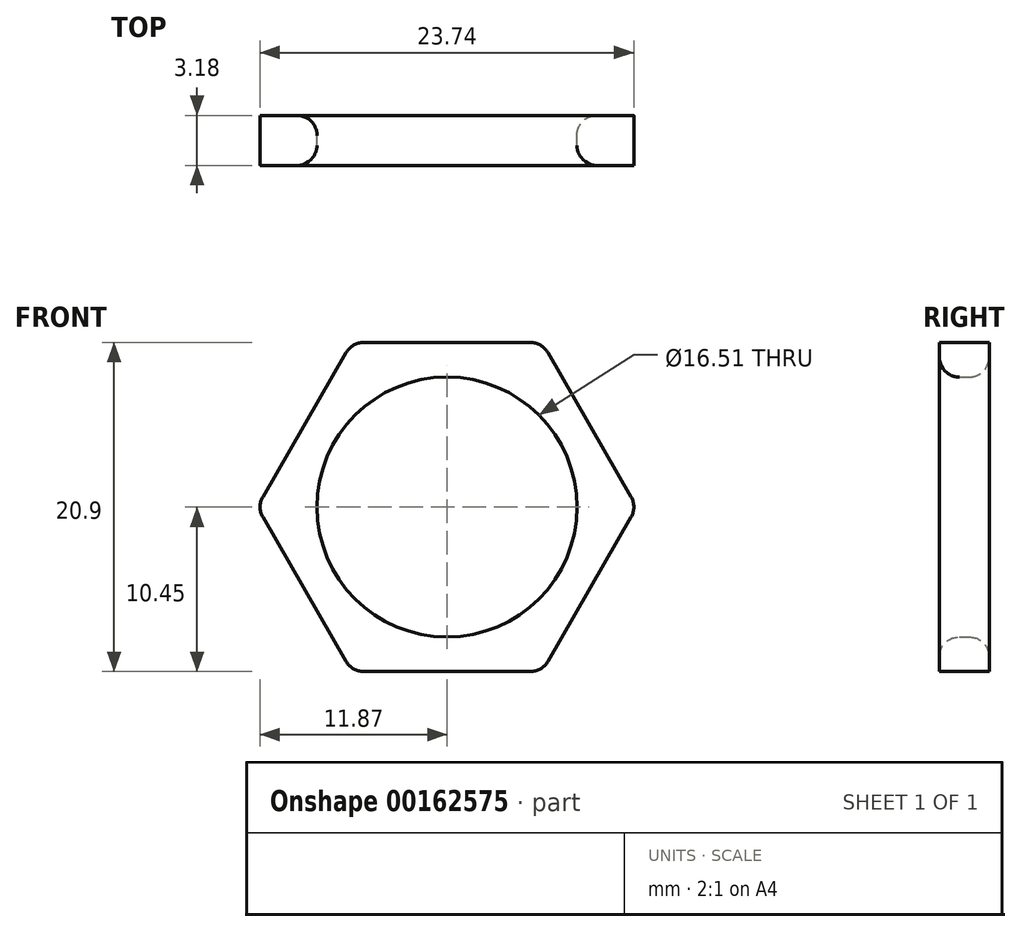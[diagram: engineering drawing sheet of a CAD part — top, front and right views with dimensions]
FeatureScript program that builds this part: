
annotation { "Feature Type Name" : "Feature", "Feature Type Description" : "" }
export const myFeature = defineFeature(function(context is Context, id is Id, definition is map)
    precondition{}
    {
        {
            var Q0;
            Q0=qCreatedBy(makeId("Front.planeOp"),FACE);
            var sketch = newSketch(context, id + "F0", { "sketchPlane" : qUnion([Q0])});
            skCircle(sketch, "E0.cCircle", {"center": v(0, 0) * mm, "radius": 12.07 * mm, "construction": true});
            skLineSegment(sketch, "E0.0", {"start": v(-12.06, 0) * mm, "end": v(-6.03, 10.45) * mm});
            skLineSegment(sketch, "E0.1", {"start": v(-6.03, 10.45) * mm, "end": v(6.03, 10.45) * mm});
            skLineSegment(sketch, "E0.2", {"start": v(6.03, 10.45) * mm, "end": v(12.07, 0) * mm});
            skLineSegment(sketch, "E0.3", {"start": v(12.06, 0) * mm, "end": v(6.03, -10.45) * mm});
            skLineSegment(sketch, "E0.4", {"start": v(6.03, -10.45) * mm, "end": v(-6.03, -10.45) * mm});
            skLineSegment(sketch, "E0.5", {"start": v(-6.03, -10.45) * mm, "end": v(-12.07, 0) * mm});
            skPoint(sketch, "E1.3.end.orphan", {"position": v(0, 8.28) * mm});
            skCircle(sketch, "E2", {"center": v(0, 0) * mm, "radius": 8.26 * mm});
            skSolve(sketch);
        }
        {
            var Q0;
            Q0 = qSketchRegion(id + "F0", true);
            extrude(context, id + "F2", {"entities" : qUnion([Q0]), "depth" : 3.17 * mm});
        }
        {
            var Q0;
            Q0=makeQuery(id+"F2.opExtrude","CAP_EDGE",EDGE,{"disambiguationData":[OSD([sQuery(id+"F0.wireOp",EDGE,"E2")])],"isStart":false});
            var Q1;
            Q1=makeQuery(id+"F2.opExtrude","CAP_EDGE",EDGE,{"disambiguationData":[OSD([sQuery(id+"F0.wireOp",EDGE,"E2")])],"isStart":true});
            var Q2;
            Q2=makeQuery(id+"F2.opExtrude","SWEPT_EDGE",EDGE,{"disambiguationData":[OSD([sQuery(id+"F0.wireOp",EDGE,"E0.3"),sQuery(id+"F0.wireOp",EDGE,"E0.4")])]});
            var Q3;
            Q3=makeQuery(id+"F2.opExtrude","SWEPT_EDGE",EDGE,{"disambiguationData":[OSD([sQuery(id+"F0.wireOp",EDGE,"E0.4"),sQuery(id+"F0.wireOp",EDGE,"E0.5")])]});
            var Q4;
            Q4=makeQuery(id+"F2.opExtrude","SWEPT_EDGE",EDGE,{"disambiguationData":[OSD([sQuery(id+"F0.wireOp",EDGE,"E0.0"),sQuery(id+"F0.wireOp",EDGE,"E0.5")])]});
            var Q5;
            Q5=makeQuery(id+"F2.opExtrude","SWEPT_EDGE",EDGE,{"disambiguationData":[OSD([sQuery(id+"F0.wireOp",EDGE,"E0.2"),sQuery(id+"F0.wireOp",EDGE,"E0.3")])]});
            var Q6;
            Q6=makeQuery(id+"F2.opExtrude","SWEPT_EDGE",EDGE,{"disambiguationData":[OSD([sQuery(id+"F0.wireOp",EDGE,"E0.1"),sQuery(id+"F0.wireOp",EDGE,"E0.2")])]});
            var Q7;
            Q7=makeQuery(id+"F2.opExtrude","SWEPT_EDGE",EDGE,{"disambiguationData":[OSD([sQuery(id+"F0.wireOp",EDGE,"E0.0"),sQuery(id+"F0.wireOp",EDGE,"E0.1")])]});
            fillet(context, id + "F1", {"entities" : qUnion([Q0, Q1, Q2, Q3, Q4, Q5, Q6, Q7]), "radius" : 1.27 * mm, "tangentPropagation" : true, "allowEdgeOverflow" : false});
        }
    });
